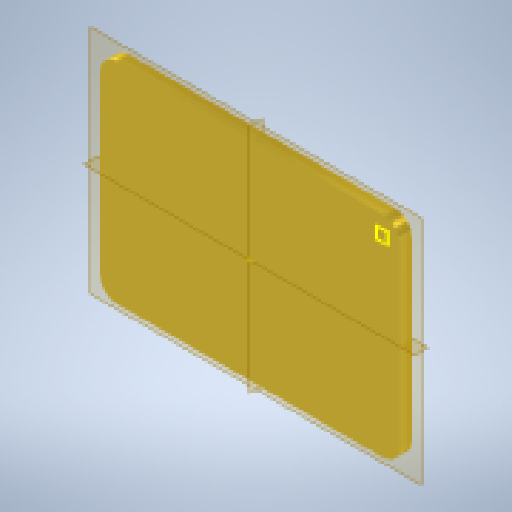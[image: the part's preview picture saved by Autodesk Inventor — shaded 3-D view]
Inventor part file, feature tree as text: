
AUTODESK INVENTOR PART (.ipt)
format: ipt  version: 2025.2 (Build 292293000, 293)  size: 262,656 bytes
history: native  units: mm
features: other x10, extrude x2, sketch x2, fillet x1
ambient origin geometry x8: Origin, YZ Plane, XZ Plane, XY Plane, X Axis, Y Axis, Z Axis, Center Point
bodies: Body1 (feature_tree)
feature tree (15):
  other  "Sólido1"
  extrude  "Extrusão1"  Depth=350.0mm
  fillet  "Arredondamento1"  Radius=20.0mm
  extrude  "Extrusão2"  Depth=0.2mm
  sketch  "Esboço1"  dims[d0=500.0mm d1=350.0mm d2=20.0mm d3=0.0mm]
  sketch  "Esboço2"  dims[d4=30.0mm d5=0.2mm d6=0.2mm d7=0.2mm d8=0.2mm d9=20.0mm d10=0.0mm d11=0.5mm d12=0.872665mm d13=0.5mm d14=0.872665mm]
  other  "Referência1"
  other  "Referência2"
  other  "Referência3"
  other  "Referência4"
  other  "Sessao8_07_04_2025_999_0001.iam"
  other  "Sessao8_07_04_2025_0002_0001:3"
  other  "Sessao8_07_04_2025_0002_0001:4"
  other  "Sessao8_07_04_2025_0002_0001:1"
  other  "Sessao8_07_04_2025_0002_0001:2"
